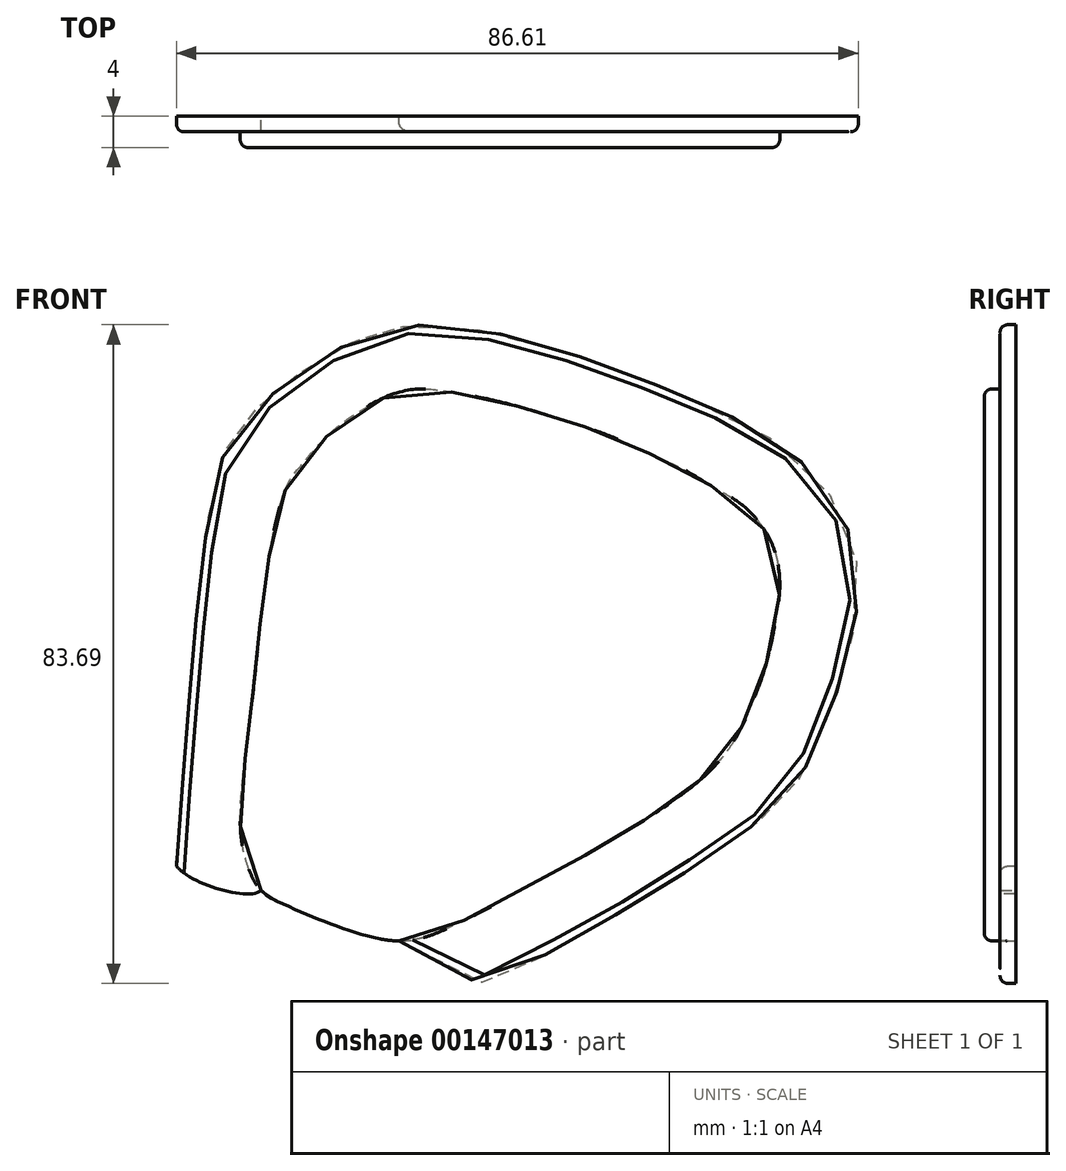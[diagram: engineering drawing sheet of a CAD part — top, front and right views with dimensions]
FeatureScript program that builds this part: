
annotation { "Feature Type Name" : "Feature", "Feature Type Description" : "" }
export const myFeature = defineFeature(function(context is Context, id is Id, definition is map)
    precondition{}
    {
        {
            var Q0;
            Q0=qCreatedBy(makeId("Front.planeOp"),FACE);
            var sketch = newSketch(context, id + "F0", { "sketchPlane" : qUnion([Q0])});
            skFitSpline(sketch, "E0", {"points": [v(-147.32, 112.48) * mm, v(-141.66, 111.35) * mm, v(-134.72, 109.36) * mm, v(-127.92, 107.1) * mm, v(-122.69, 104.83) * mm, v(-117.94, 102.57) * mm, v(-114.76, 100.66) * mm, v(-111.29, 98.6) * mm, v(-108.6, 95.98) * mm, v(-107.04, 93.43) * mm, v(-106.26, 90.96) * mm, v(-105.98, 87.7) * mm, v(-106.47, 83.66) * mm, v(-107.77, 77.76) * mm, v(-109.48, 73.05) * mm, v(-110.98, 69.65) * mm, v(-113.18, 66.24) * mm, v(-115.98, 63.34) * mm, v(-120.09, 60.24) * mm, v(-127.8, 55.33) * mm, v(-134.4, 51.72) * mm, v(-141.82, 47.62) * mm, v(-146.72, 45.12) * mm, v(-150.63, 43.41) * mm, v(-154.33, 42.81) * mm, v(-158.24, 43.41) * mm, v(-163.64, 45.22) * mm, v(-168.65, 47.32) * mm, v(-171.85, 49.22) * mm, v(-173.55, 52.33) * mm, v(-174.46, 56.63) * mm, v(-174.16, 63.74) * mm, v(-173.05, 72.85) * mm, v(-171.65, 85.87) * mm, v(-170.35, 94.38) * mm, v(-169.35, 98.48) * mm, v(-168.25, 101.29) * mm, v(-166.35, 103.69) * mm, v(-164.54, 105.8) * mm, v(-161.94, 108.3) * mm, v(-159.14, 110.2) * mm, v(-156.53, 111.7) * mm, v(-153.13, 112.8) * mm, v(-150.33, 112.9) * mm, v(-147.32, 112.48) * mm]});
            skFitSpline(sketch, "E1", {"points": [v(-182.61, 52.33) * mm, v(-181.41, 68.51) * mm, v(-178.73, 95.44) * mm, v(-176.78, 104.14) * mm, v(-174.75, 107.93) * mm, v(-170.68, 112) * mm, v(-166.7, 115.15) * mm, v(-161.7, 118.2) * mm, v(-157.63, 119.96) * mm, v(-151.98, 121.07) * mm, v(-140.05, 119.6) * mm, v(-122.93, 113.95) * mm, v(-106.55, 106.27) * mm, v(-98.96, 98.5) * mm, v(-96.18, 90.63) * mm, v(-96.74, 81.65) * mm, v(-100.44, 69.9) * mm, v(-103.5, 63.42) * mm, v(-106.64, 59.63) * mm, v(-115.43, 53.24) * mm, v(-124.04, 47.7) * mm, v(-135.79, 41.03) * mm, v(-142.45, 37.42) * mm, v(-154.33, 42.81) * mm], "startDerivative": vector(18.24, 257.74) * mm, "endDerivative": vector(-260.09, 165.04) * mm});
            skFitSpline(sketch, "E2", {"points": [v(-182.61, 52.33) * mm, v(-171.85, 49.22) * mm], "startDerivative": vector(4.72, -6.69) * mm, "endDerivative": vector(4.8, 4.31) * mm});
            skSolve(sketch);
        }
        {
            var Q0;
            {var subQ0=sQuery(id+"F0.wireOp",EDGE,"E1");Q0=makeQuery(id+"F0.imprint","IMPRINT",FACE,{"disambiguationData":[TD([[makeQuery(id+"F0.imprint","IMPRINT",EDGE,{"derivedFrom":subQ0}),-1.0]])]});}
            extrude(context, id + "F1", {"entities" : qUnion([Q0]), "depth" : 2 * mm, "offsetDistance" : 25 * mm});
        }
        {
            var Q0;
            {var subQ0=sQuery(id+"F0.wireOp",EDGE,"E0");var subQ1=makeQuery(id+"F0.imprint","INTERSECT",VERTEX,{"derivedFrom":[subQ0,sQuery(id+"F0.wireOp",EDGE,"E1")]});Q0=makeQuery(id+"F0.imprint","IMPRINT",FACE,{"disambiguationData":[TD([[makeQuery(id+"F0.imprint","IMPRINT",EDGE,{"disambiguationData":[TD([[subQ1,-1.0]])],"derivedFrom":subQ0}),-1.0]])]});}
            extrude(context, id + "F2", {"entities" : qUnion([Q0]), "operationType" : NewBodyOperationType.ADD, "depth" : 4 * mm, "offsetDistance" : 25 * mm});
        }
        {
            var Q0;
            Q0=makeQuery(id+"F2.opExtrude","CAP_EDGE",EDGE,{"disambiguationData":[OSD([sQuery(id+"F0.wireOp",EDGE,"E0")])],"isStart":false});
            var Q1;
            Q1=makeQuery(id+"F1.opExtrude","CAP_EDGE",EDGE,{"disambiguationData":[OSD([sQuery(id+"F0.wireOp",EDGE,"E1")])],"isStart":false});
            fillet(context, id + "F3", {"entities" : qUnion([Q0, Q1]), "radius" : 1 * mm, "tangentPropagation" : true, "allowEdgeOverflow" : false});
        }
    });
